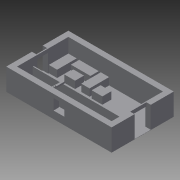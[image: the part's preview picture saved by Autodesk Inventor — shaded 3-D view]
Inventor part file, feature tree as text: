
AUTODESK INVENTOR PART (.ipt)
format: ipt  version: 2014 (Build 180170000, 170)  size: 372,736 bytes
history: native  units: in
note: dims shown in document units (in); Inventor stores cm internally (conversion verified against a paired STEP export)
features: extrude x8, sketch x5, projected_geometry x3, other x3
ambient origin geometry x8: Origin, YZ Plane, XZ Plane, XY Plane, X Axis, Y Axis, Z Axis, Center Point
bodies: Body1 (feature_tree)
feature tree (19):
  extrude  "Extrusion9"  Depth=150.0in
  extrude  "Extrusion10"  Depth=216.0in
  extrude  "Stairs"  Depth=24.0in
  extrude  "Doorways"  Depth=72.0in
  extrude  "Window"  Depth=24.0in
  extrude  "Furniture+Pallets"  Depth=32.0in
  extrude  "Instrumentation"  Depth=4.5in
  extrude  "FurnitureOnly"  TaperAngle=0.0deg  [1 undecoded]
  sketch  "Sketch1"  dims[d0=288.0in d1=480.0in d2=432.0in d3=240.0in d5=132.0in d7=150.0in]
  sketch  "Sketch8"  dims[d11=57.0in d17=216.0in]
  projected_geometry  "Projected Loop5"
  sketch  "Sketch9"  dims[d18=276.0in d19=24.0in]
  projected_geometry  "Projected Loop6"
  sketch  "Sketch10"  dims[d20=24.0in d23=72.0in]
  sketch  "Sketch11"  dims[d24=102.0in d25=24.0in d27=432.0in d28=4.5in d29=0.0in d30=168.0in d34=48.0in d35=114.0in d36=24.0in d46=35.0in d105=35.0in d106=468.0in d107=96.0in d108=0.0in d109=1.0in d110=0.0in d113=7.5in d115=7.25in d116=28.5in d117=7.5in d118=7.25in d119=7.5in d120=7.25in d121=7.5in d122=7.25in d123=7.5in d124=7.25in d125=7.5in d126=7.25in d127=7.5in d128=7.25in d129=7.5in d130=7.25in d131=7.5in d132=7.25in d133=7.5in d134=7.25in d135=7.5in d136=7.25in d137=7.5in d138=7.25in d139=7.5in d140=7.25in d141=7.5in d142=7.25in d143=16.0in d144=0.0in d145=48.0in d147=48.0in d148=32.0in d150=16.0in d151=0.0in d154=7.25in d155=7.5in d161=12.0in d163=12.0in d164=140.0in d165=280.0in d166=12.0in d172=12.0in d173=12.0in d192=6.0in d193=6.0in d194=6.0in d195=18.0in d196=18.0in d197=18.0in d198=18.0in d227=17.5in d228=17.5in d229=6.0in d230=6.0in d231=18.0in d234=12.0in d235=12.0in d236=6.0in d237=12.0in d238=12.0in d239=6.0in d240=18.0in d241=4.5in d242=4.5in d243=16.0in d244=0.0in d247=39.3701in d248=47.2441in d249=39.3701in d250=47.2441in d251=50.0in d252=72.0in d253=12.0in d254=87.0in d255=37.0in d256=37.0in d257=37.0in d258=87.0in d259=48.0in d260=144.0in d261=87.0in d262=37.0in d263=87.0in d264=37.0in d265=87.0in d266=37.0in d267=48.0in d268=48.0in d269=1.0in d270=0.0in d271=32.0in d272=0.0in d273=32.0in d274=0.0in]
  other  "Instruments"
  projected_geometry  "Projected Loop8"
  other  "Furniture1"
  other  "Furniture2"
note: 1 required parameter value undecoded (feature->parameter linkage not recoverable at this tier; creation-order binding heuristic only, values carry confidence <= 0.55)
